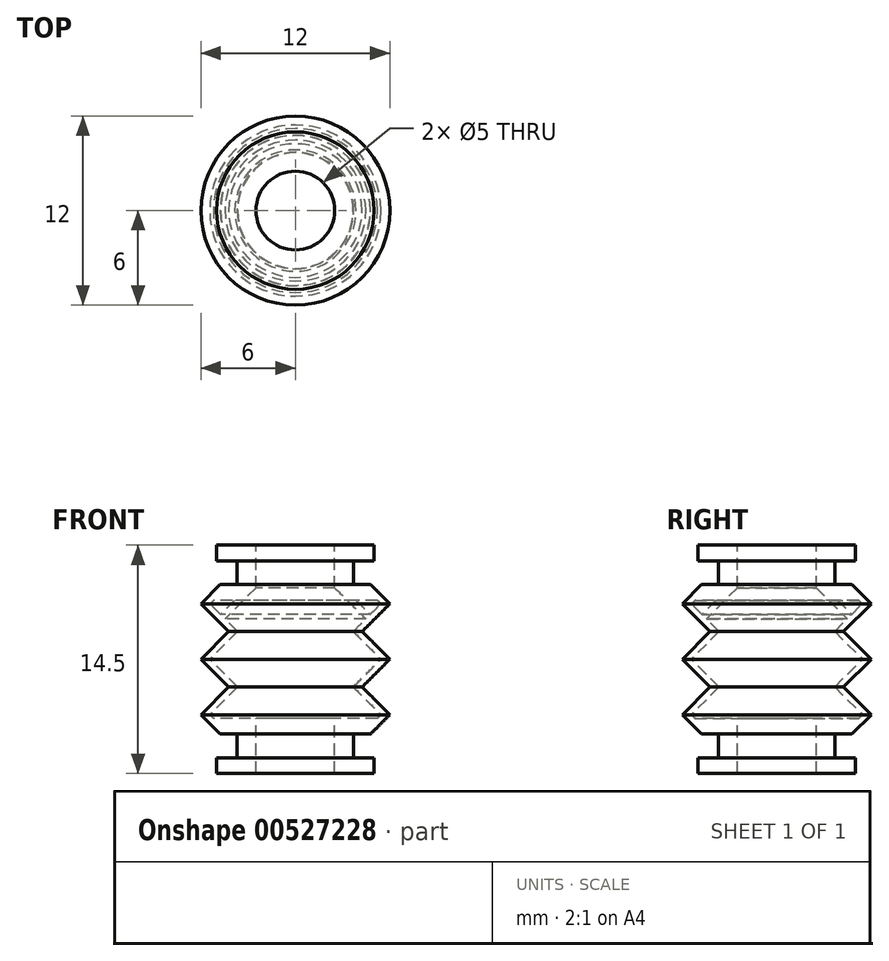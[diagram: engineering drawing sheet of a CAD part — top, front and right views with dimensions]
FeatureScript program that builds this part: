
annotation { "Feature Type Name" : "Feature", "Feature Type Description" : "" }
export const myFeature = defineFeature(function(context is Context, id is Id, definition is map)
    precondition{}
    {
        {
            var Q0;
            Q0=qCreatedBy(makeId("Front.planeOp"),FACE);
            var sketch = newSketch(context, id + "F0", { "sketchPlane" : qUnion([Q0])});
            skLineSegment(sketch, "E0", {"start": v(-2.5, 7.25) * mm, "end": v(-5, 7.25) * mm});
            skLineSegment(sketch, "E1", {"start": v(-5, 7.25) * mm, "end": v(-5, 6.25) * mm});
            skLineSegment(sketch, "E2", {"start": v(-5, 6.25) * mm, "end": v(-3.7, 6.25) * mm});
            skLineSegment(sketch, "E3", {"start": v(-3.7, 6.25) * mm, "end": v(-3.7, 4.75) * mm});
            skLineSegment(sketch, "E4", {"start": v(-4.77, 4.75) * mm, "end": v(-6, 3.52) * mm});
            skLineSegment(sketch, "E5", {"start": v(-6, 3.52) * mm, "end": v(-4.24, 1.76) * mm});
            skLineSegment(sketch, "E6", {"start": v(-4.24, 1.76) * mm, "end": v(-6, 0) * mm});
            skLineSegment(sketch, "E7", {"start": v(-3.7, 4.75) * mm, "end": v(-4.77, 4.75) * mm});
            skLineSegment(sketch, "E8", {"start": v(0, 8.81) * mm, "end": v(0, -10.41) * mm, "construction": true});
            skLineSegment(sketch, "E9", {"start": v(-5.43, 0) * mm, "end": v(-3.67, 1.76) * mm});
            skLineSegment(sketch, "E10", {"start": v(-5.43, 3.52) * mm, "end": v(-5.2, 3.75) * mm});
            skLineSegment(sketch, "E11", {"start": v(-3.67, 1.76) * mm, "end": v(-4.47, 2.56) * mm});
            skLineSegment(sketch, "E12", {"start": v(-2.5, 7.25) * mm, "end": v(-2.5, 4.54) * mm});
            skLineSegment(sketch, "E13.MirrorCS", {"start": v(-2.5, -7.25) * mm, "end": v(-5, -7.25) * mm});
            skLineSegment(sketch, "E14.MirrorCS", {"start": v(-5, -7.25) * mm, "end": v(-5, -6.25) * mm});
            skLineSegment(sketch, "E15.MirrorCS", {"start": v(-2.5, -7.25) * mm, "end": v(-2.5, -3.75) * mm});
            skLineSegment(sketch, "E16.MirrorCS", {"start": v(-3.7, -6.25) * mm, "end": v(-3.7, -4.75) * mm});
            skLineSegment(sketch, "E17.MirrorCS", {"start": v(-3.7, -4.75) * mm, "end": v(-4.77, -4.75) * mm});
            skLineSegment(sketch, "E18.MirrorCS", {"start": v(-2.5, -3.75) * mm, "end": v(-5.2, -3.75) * mm});
            skLineSegment(sketch, "E19.MirrorCS", {"start": v(-4.77, -4.75) * mm, "end": v(-6, -3.52) * mm});
            skLineSegment(sketch, "E20.MirrorCS", {"start": v(-5.43, -3.52) * mm, "end": v(-5.2, -3.75) * mm});
            skLineSegment(sketch, "E21.MirrorCS", {"start": v(-6, -3.52) * mm, "end": v(-4.24, -1.76) * mm});
            skLineSegment(sketch, "E22.MirrorCS", {"start": v(-3.67, -1.76) * mm, "end": v(-5.43, -3.52) * mm});
            skLineSegment(sketch, "E23.MirrorCS", {"start": v(-5.43, 0) * mm, "end": v(-3.67, -1.76) * mm});
            skLineSegment(sketch, "E24.MirrorCS", {"start": v(-4.24, -1.76) * mm, "end": v(-6, 0) * mm});
            skLineSegment(sketch, "E25", {"start": v(-5, -6.25) * mm, "end": v(-3.7, -6.25) * mm});
            skLineSegment(sketch, "E26", {"start": v(-4.76, 2.85) * mm, "end": v(-3.85, 3.75) * mm});
            skLineSegment(sketch, "E27", {"start": v(-4.47, 2.56) * mm, "end": v(-2.5, 4.54) * mm});
            skLineSegment(sketch, "E28.trimOffspring", {"start": v(-4.76, 2.85) * mm, "end": v(-5.43, 3.52) * mm});
            skLineSegment(sketch, "E29.trimOffspring", {"start": v(-3.85, 3.75) * mm, "end": v(-5.2, 3.75) * mm});
            skSolve(sketch);
        }
        {
            var Q0;
            Q0=makeQuery(id+"F0.imprint","IMPRINT",FACE,{"disambiguationData":[TD([[makeQuery(id+"F0.imprint","IMPRINT",EDGE,{"derivedFrom":sQuery(id+"F0.wireOp",EDGE,"E0")}),1.0]])]});
            var Q1;
            Q1=sQuery(id+"F0.wireOp",EDGE,"E8");
            revolve(context, id + "F1", {"entities" : qUnion([Q0]), "axis" : qUnion([Q1]), "revolveType" : RevolveType.FULL});
        }
    });
